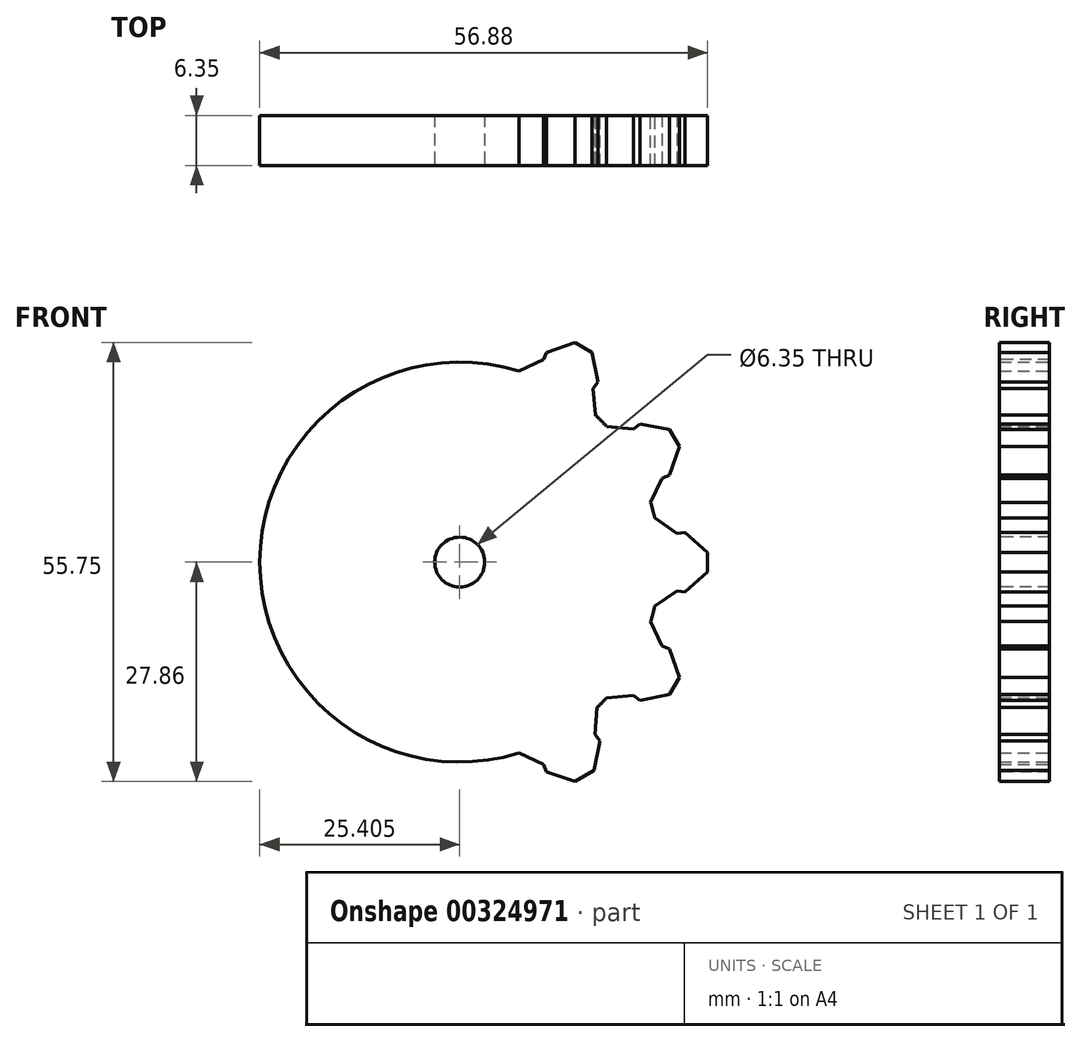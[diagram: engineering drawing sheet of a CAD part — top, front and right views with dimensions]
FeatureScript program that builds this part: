
annotation { "Feature Type Name" : "Feature", "Feature Type Description" : "" }
export const myFeature = defineFeature(function(context is Context, id is Id, definition is map)
    precondition{}
    {
        {
            var Q0;
            Q0=qCreatedBy(makeId("Front.planeOp"),FACE);
            var sketch = newSketch(context, id + "F0", { "sketchPlane" : qUnion([Q0])});
            skCircle(sketch, "E0", {"center": v(-47.62, 0) * mm, "radius": 3.18 * mm});
            skSolve(sketch);
        }
        {
            var Q0;
            Q0 = qSketchRegion(id + "F0", true);
            extrude(context, id + "F1", {"entities" : qUnion([Q0]), "endBound" : BoundingType.SYMMETRIC, "depth" : 31.75 * mm});
        }
        {
            var Q0;
            Q0=qCreatedBy(makeId("Front.planeOp"),FACE);
            var sketch = newSketch(context, id + "F2", { "sketchPlane" : qUnion([Q0])});
            skCircle(sketch, "E1", {"center": v(-47.62, 0) * mm, "radius": 25.4 * mm});
            skSolve(sketch);
        }
        {
            var Q0;
            Q0 = qSketchRegion(id + "F2", true);
            var Q1;
            {var subQ0=sQuery(id+"F2.wireOp",EDGE,"0KpzJK3X-RqZ1-LjoC-YCLd-mAtgLIeUfhWk");var subQ1=makeQuery(id+"FyZQcZ8PwhC0EKz_0.opExtrude","CAP_EDGE",EDGE,{"disambiguationData":[OSD([sQuery(id+"FS2qxtXSqbEyFNz_0.wireOp",EDGE,"Z0xn4rbn-BjCm-V79e-58Z2-rPe6abgB0Axc"),sQuery(id+"FS2qxtXSqbEyFNz_0.wireOp",EDGE,"XHgkERbV-JrNv-KUjZ-BbE3-05hLdR0Ggr4t")])],"isStart":false});var subQ2=makeQuery(id+"F2.imprint","INTERSECT",VERTEX,{"disambiguationData":[OD(0.0)],"derivedFrom":[subQ1,subQ0]});Q1=makeQuery(id+"F2.imprint","IMPRINT",FACE,{"disambiguationData":[TD([[makeQuery(id+"F2.imprint","IMPRINT",EDGE,{"disambiguationData":[TD([[subQ2,1.0]])],"derivedFrom":subQ0}),1.0]])]});}
            extrude(context, id + "F3", {"entities" : qUnion([Q0, Q1]), "depth" : 6.35 * mm});
        }
        {
            var Q0;
            Q0=qCreatedBy(makeId("Front.planeOp"),FACE);
            var sketch = newSketch(context, id + "F4", { "sketchPlane" : qUnion([Q0])});
            skPoint(sketch, "E2", {"position": v(-22.23, 0) * mm});
            skLineSegment(sketch, "E3", {"start": v(-28.57, 11) * mm, "end": v(-19.03, 16.5) * mm});
            skPoint(sketch, "E4", {"position": v(-25.63, 12.7) * mm});
            skPoint(sketch, "E5", {"position": v(-25.64, -12.72) * mm});
            skLineSegment(sketch, "E6", {"start": v(-47.63, 0) * mm, "end": v(-34.92, 22) * mm, "construction": true});
            skLineSegment(sketch, "E7", {"start": v(-47.63, 0) * mm, "end": v(-31.75, 27.5) * mm});
            skLineSegment(sketch, "E8", {"start": v(-47.63, 0) * mm, "end": v(-34.92, -22) * mm, "construction": true});
            skLineSegment(sketch, "E9", {"start": v(-47.63, 0) * mm, "end": v(-47.63, 33.02) * mm, "construction": true});
            skLineSegment(sketch, "E10", {"start": v(-47.63, 33.02) * mm, "end": v(-47.63, -33.02) * mm, "construction": true});
            skLineSegment(sketch, "E11", {"start": v(-28.04, -24.99) * mm, "end": v(-35.47, -29.33) * mm});
            skLineSegment(sketch, "E12", {"start": v(-47.62, 0) * mm, "end": v(-22.44, -19.33) * mm});
            skLineSegment(sketch, "E13", {"start": v(-27.47, -15.46) * mm, "end": v(-22.44, -19.33) * mm});
            skLineSegment(sketch, "E14", {"start": v(-47.63, 0) * mm, "end": v(-18.3, -12.15) * mm});
            skLineSegment(sketch, "E15", {"start": v(-47.63, 0) * mm, "end": v(-16.15, -4.14) * mm});
            skLineSegment(sketch, "E16", {"start": v(-16.15, -4.14) * mm, "end": v(-16.15, 4.14) * mm});
            skLineSegment(sketch, "E17", {"start": v(-16.15, 4.14) * mm, "end": v(-47.63, 0) * mm});
            skLineSegment(sketch, "E18", {"start": v(-22.44, -19.33) * mm, "end": v(-18.3, -12.15) * mm});
            skLineSegment(sketch, "E19", {"start": v(-47.63, 0) * mm, "end": v(-18.3, 12.15) * mm});
            skLineSegment(sketch, "E20", {"start": v(-47.63, 0) * mm, "end": v(-22.44, 19.33) * mm});
            skLineSegment(sketch, "E21", {"start": v(-22.44, 19.33) * mm, "end": v(-18.3, 12.15) * mm});
            skLineSegment(sketch, "E22", {"start": v(-47.63, 0) * mm, "end": v(-28.3, 25.19) * mm});
            skLineSegment(sketch, "E23", {"start": v(-47.63, 0) * mm, "end": v(-35.47, 29.33) * mm});
            skLineSegment(sketch, "E24", {"start": v(-35.47, 29.33) * mm, "end": v(-28.3, 25.19) * mm});
            skLineSegment(sketch, "E25", {"start": v(-37.9, -23.47) * mm, "end": v(-38.6, -21.85) * mm});
            skLineSegment(sketch, "E26", {"start": v(-33.25, -18.5) * mm, "end": v(-32.3, -19.98) * mm});
            skLineSegment(sketch, "E27", {"start": v(-47.63, 0) * mm, "end": v(-35.47, -29.33) * mm});
            skLineSegment(sketch, "E28", {"start": v(-47.63, 0) * mm, "end": v(-28.04, -24.99) * mm});
            skSolve(sketch);
        }
        {
            var Q0;
            {var subQ0=sQuery(id+"F4.wireOp",EDGE,"E22");Q0=makeQuery(id+"F4.imprint","IMPRINT",FACE,{"disambiguationData":[TD([[makeQuery(id+"F4.imprint","IMPRINT",EDGE,{"derivedFrom":subQ0}),1.0]])]});}
            var Q1;
            {var subQ0=sQuery(id+"F4.wireOp",EDGE,"E23");Q1=makeQuery(id+"F4.imprint","IMPRINT",FACE,{"disambiguationData":[TD([[makeQuery(id+"F4.imprint","IMPRINT",EDGE,{"derivedFrom":subQ0}),-1.0]])]});}
            var Q2;
            {var subQ0=sQuery(id+"F4.wireOp",EDGE,"E19");Q2=makeQuery(id+"F4.imprint","IMPRINT",FACE,{"disambiguationData":[TD([[makeQuery(id+"F4.imprint","IMPRINT",EDGE,{"derivedFrom":subQ0}),1.0]])]});}
            var Q3;
            {var subQ0=sQuery(id+"F4.wireOp",EDGE,"E15");Q3=makeQuery(id+"F4.imprint","IMPRINT",FACE,{"disambiguationData":[TD([[makeQuery(id+"F4.imprint","IMPRINT",EDGE,{"derivedFrom":subQ0}),1.0]])]});}
            var Q4;
            Q4=makeQuery(id+"F4.imprint","IMPRINT",FACE,{"disambiguationData":[TD([[makeQuery(id+"F4.imprint","IMPRINT",EDGE,{"derivedFrom":sQuery(id+"F4.wireOp",EDGE,"E12")}),1.0]])]});
            var Q5;
            {var subQ0=sQuery(id+"F4.wireOp",EDGE,"E11");Q5=makeQuery(id+"F4.imprint","IMPRINT",FACE,{"disambiguationData":[TD([[makeQuery(id+"F4.imprint","IMPRINT",EDGE,{"derivedFrom":subQ0}),-1.0]])]});}
            extrude(context, id + "F5", {"entities" : qUnion([Q0, Q1, Q2, Q3, Q4, Q5]), "operationType" : NewBodyOperationType.ADD, "depth" : 6.35 * mm});
        }
        {
            var Q0;
            Q0=makeQuery(id+"F5.opExtrude","SWEPT_EDGE",EDGE,{"disambiguationData":[OSD([sQuery(id+"F4.wireOp",EDGE,"E11"),sQuery(id+"F4.wireOp",EDGE,"E27")])]});
            var Q1;
            Q1=makeQuery(id+"F5.opExtrude","SWEPT_EDGE",EDGE,{"disambiguationData":[OSD([sQuery(id+"F4.wireOp",EDGE,"E11"),sQuery(id+"F4.wireOp",EDGE,"E28")])]});
            var Q2;
            Q2=makeQuery(id+"F5.opExtrude","SWEPT_EDGE",EDGE,{"disambiguationData":[OSD([sQuery(id+"F4.wireOp",EDGE,"E13"),sQuery(id+"F4.wireOp",EDGE,"E18")])]});
            var Q3;
            Q3=makeQuery(id+"F5.opExtrude","SWEPT_EDGE",EDGE,{"disambiguationData":[OSD([sQuery(id+"F4.wireOp",EDGE,"E14"),sQuery(id+"F4.wireOp",EDGE,"E18")])]});
            var Q4;
            Q4=makeQuery(id+"F5.opExtrude","SWEPT_EDGE",EDGE,{"disambiguationData":[OSD([sQuery(id+"F4.wireOp",EDGE,"E16"),sQuery(id+"F4.wireOp",EDGE,"E17")])]});
            var Q5;
            Q5=makeQuery(id+"F5.opExtrude","SWEPT_EDGE",EDGE,{"disambiguationData":[OSD([sQuery(id+"F4.wireOp",EDGE,"E15"),sQuery(id+"F4.wireOp",EDGE,"E16")])]});
            var Q6;
            Q6=makeQuery(id+"F5.opExtrude","SWEPT_EDGE",EDGE,{"disambiguationData":[OSD([sQuery(id+"F4.wireOp",EDGE,"E19"),sQuery(id+"F4.wireOp",EDGE,"E21")])]});
            var Q7;
            Q7=makeQuery(id+"F5.opExtrude","SWEPT_EDGE",EDGE,{"disambiguationData":[OSD([sQuery(id+"F4.wireOp",EDGE,"E20"),sQuery(id+"F4.wireOp",EDGE,"E21")])]});
            var Q8;
            Q8=makeQuery(id+"F5.opExtrude","SWEPT_EDGE",EDGE,{"disambiguationData":[OSD([sQuery(id+"F4.wireOp",EDGE,"E22"),sQuery(id+"F4.wireOp",EDGE,"E24")])]});
            var Q9;
            Q9=makeQuery(id+"F5.opExtrude","SWEPT_EDGE",EDGE,{"disambiguationData":[OSD([sQuery(id+"F4.wireOp",EDGE,"E23"),sQuery(id+"F4.wireOp",EDGE,"E24")])]});
            var Q10;
            Q10=makeQuery(id+"F5.boolean.opBoolean","INTERSECT",EDGE,{"derivedFrom":[makeQuery(id+"F3.opExtrude","SWEPT_FACE",FACE,{"disambiguationData":[OSD([sQuery(id+"F2.wireOp",EDGE,"E1")])]}),makeQuery(id+"F5.opExtrude","SWEPT_FACE",FACE,{"disambiguationData":[OSD([sQuery(id+"F4.wireOp",EDGE,"E28")])]})]});
            var Q11;
            Q11=makeQuery(id+"F5.boolean.opBoolean","INTERSECT",EDGE,{"derivedFrom":[makeQuery(id+"F3.opExtrude","SWEPT_FACE",FACE,{"disambiguationData":[OSD([sQuery(id+"F2.wireOp",EDGE,"E1")])]}),makeQuery(id+"F5.opExtrude","SWEPT_FACE",FACE,{"disambiguationData":[OSD([sQuery(id+"F4.wireOp",EDGE,"E12"),sQuery(id+"F4.wireOp",EDGE,"E13")])]})]});
            var Q12;
            Q12=makeQuery(id+"F5.boolean.opBoolean","INTERSECT",EDGE,{"derivedFrom":[makeQuery(id+"F3.opExtrude","SWEPT_FACE",FACE,{"disambiguationData":[OSD([sQuery(id+"F2.wireOp",EDGE,"E1")])]}),makeQuery(id+"F5.opExtrude","SWEPT_FACE",FACE,{"disambiguationData":[OSD([sQuery(id+"F4.wireOp",EDGE,"E14")])]})]});
            var Q13;
            Q13=makeQuery(id+"F5.boolean.opBoolean","INTERSECT",EDGE,{"derivedFrom":[makeQuery(id+"F3.opExtrude","SWEPT_FACE",FACE,{"disambiguationData":[OSD([sQuery(id+"F2.wireOp",EDGE,"E1")])]}),makeQuery(id+"F5.opExtrude","SWEPT_FACE",FACE,{"disambiguationData":[OSD([sQuery(id+"F4.wireOp",EDGE,"E15")])]})]});
            var Q14;
            Q14=makeQuery(id+"F5.boolean.opBoolean","INTERSECT",EDGE,{"derivedFrom":[makeQuery(id+"F3.opExtrude","SWEPT_FACE",FACE,{"disambiguationData":[OSD([sQuery(id+"F2.wireOp",EDGE,"E1")])]}),makeQuery(id+"F5.opExtrude","SWEPT_FACE",FACE,{"disambiguationData":[OSD([sQuery(id+"F4.wireOp",EDGE,"E19")])]})]});
            var Q15;
            Q15=makeQuery(id+"F5.boolean.opBoolean","INTERSECT",EDGE,{"derivedFrom":[makeQuery(id+"F3.opExtrude","SWEPT_FACE",FACE,{"disambiguationData":[OSD([sQuery(id+"F2.wireOp",EDGE,"E1")])]}),makeQuery(id+"F5.opExtrude","SWEPT_FACE",FACE,{"disambiguationData":[OSD([sQuery(id+"F4.wireOp",EDGE,"E22")])]})]});
            var Q16;
            Q16=makeQuery(id+"F5.boolean.opBoolean","INTERSECT",EDGE,{"derivedFrom":[makeQuery(id+"F3.opExtrude","SWEPT_FACE",FACE,{"disambiguationData":[OSD([sQuery(id+"F2.wireOp",EDGE,"E1")])]}),makeQuery(id+"F5.opExtrude","SWEPT_FACE",FACE,{"disambiguationData":[OSD([sQuery(id+"F4.wireOp",EDGE,"E17")])]})]});
            var Q17;
            Q17=makeQuery(id+"F5.boolean.opBoolean","INTERSECT",EDGE,{"derivedFrom":[makeQuery(id+"F3.opExtrude","SWEPT_FACE",FACE,{"disambiguationData":[OSD([sQuery(id+"F2.wireOp",EDGE,"E1")])]}),makeQuery(id+"F5.opExtrude","SWEPT_FACE",FACE,{"disambiguationData":[OSD([sQuery(id+"F4.wireOp",EDGE,"E20")])]})]});
            var Q18;
            Q18=makeQuery(id+"F5.boolean.opBoolean","INTERSECT",EDGE,{"derivedFrom":[makeQuery(id+"F3.opExtrude","SWEPT_FACE",FACE,{"disambiguationData":[OSD([sQuery(id+"F2.wireOp",EDGE,"E1")])]}),makeQuery(id+"F5.opExtrude","SWEPT_FACE",FACE,{"disambiguationData":[OSD([sQuery(id+"F4.wireOp",EDGE,"E23")])]})]});
            var Q19;
            Q19=makeQuery(id+"F5.boolean.opBoolean","INTERSECT",EDGE,{"derivedFrom":[makeQuery(id+"F3.opExtrude","SWEPT_FACE",FACE,{"disambiguationData":[OSD([sQuery(id+"F2.wireOp",EDGE,"E1")])]}),makeQuery(id+"F5.opExtrude","SWEPT_FACE",FACE,{"disambiguationData":[OSD([sQuery(id+"F4.wireOp",EDGE,"E27")])]})]});
            chamfer(context, id + "F6", {"entities" : qUnion([Q0, Q1, Q2, Q3, Q4, Q5, Q6, Q7, Q8, Q9, Q10, Q11, Q12, Q13, Q14, Q15, Q16, Q17, Q18, Q19]), "width" : 2.54 * mm, "tangentPropagation" : true});
        }
        {
            var Q0;
            Q0=makeQuery(id+"F1.opExtrude","CAP_FACE",FACE,{"disambiguationData":[OSD([sQuery(id+"F0.wireOp",EDGE,"E0")])],"isStart":false});
            extrude(context, id + "F7", {"entities" : qUnion([Q0]), "operationType" : NewBodyOperationType.REMOVE, "oppositeDirection" : true, "depth" : 38.1 * mm});
        }
    });
